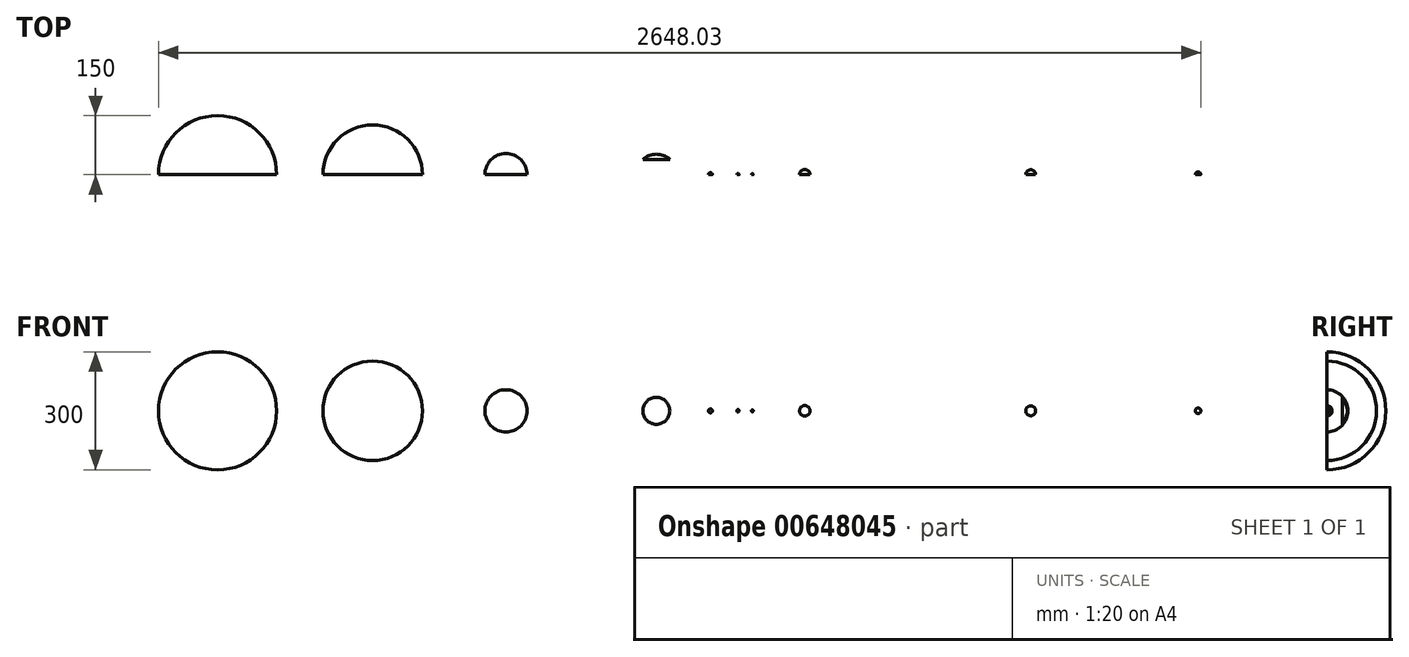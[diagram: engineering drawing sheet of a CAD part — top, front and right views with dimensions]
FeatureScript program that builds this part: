
annotation { "Feature Type Name" : "Feature", "Feature Type Description" : "" }
export const myFeature = defineFeature(function(context is Context, id is Id, definition is map)
    precondition{}
    {
        {
            var Q0;
            Q0=qCreatedBy(makeId("Front.planeOp"),FACE);
            var sketch = newSketch(context, id + "F0", { "sketchPlane" : qUnion([Q0])});
            skArc(sketch, "E0", {"start": v(-1165.18, 0) * mm, "mid": v(-1315.18, 150) * mm, "end": v(-1465.18, 0) * mm});
            skArc(sketch, "E1", {"start": v(-794.77, 0) * mm, "mid": v(-921.23, 126.45) * mm, "end": v(-1047.68, 0) * mm});
            skArc(sketch, "E2", {"start": v(-528.9, 0) * mm, "mid": v(-582.52, 53.63) * mm, "end": v(-636.15, 0) * mm});
            skArc(sketch, "E3", {"start": v(-148.68, 0) * mm, "mid": v(-200.58, 51.9) * mm, "end": v(-252.48, 0) * mm});
            skArc(sketch, "E4", {"start": v(189.86, 0) * mm, "mid": v(176.56, 13.3) * mm, "end": v(163.26, 0) * mm});
            skArc(sketch, "E5", {"start": v(763.27, 0) * mm, "mid": v(750.67, 12.6) * mm, "end": v(738.07, 0) * mm});
            skArc(sketch, "E6", {"start": v(1182.85, 0) * mm, "mid": v(1175.85, 7) * mm, "end": v(1168.85, 0) * mm});
            skLineSegment(sketch, "E7", {"start": v(-1165.18, 0) * mm, "end": v(-1465.18, 0) * mm});
            skLineSegment(sketch, "E8", {"start": v(-1047.68, 0) * mm, "end": v(-794.77, 0) * mm});
            skLineSegment(sketch, "E9", {"start": v(-636.15, 0) * mm, "end": v(-528.9, 0) * mm});
            skLineSegment(sketch, "E10", {"start": v(-252.48, 0) * mm, "end": v(-148.68, 0) * mm});
            skLineSegment(sketch, "E11", {"start": v(163.26, 0) * mm, "end": v(189.86, 0) * mm});
            skLineSegment(sketch, "E12", {"start": v(738.07, 0) * mm, "end": v(763.27, 0) * mm});
            skLineSegment(sketch, "E13", {"start": v(1168.85, 0) * mm, "end": v(1182.85, 0) * mm});
            skArc(sketch, "E14", {"start": v(-58.12, 0) * mm, "mid": v(-63.12, 5) * mm, "end": v(-68.12, 0) * mm});
            skArc(sketch, "E15", {"start": v(9.86, 0) * mm, "mid": v(6.86, 3) * mm, "end": v(3.86, 0) * mm});
            skLineSegment(sketch, "E16", {"start": v(-68.12, 0) * mm, "end": v(-58.12, 0) * mm});
            skLineSegment(sketch, "E17", {"start": v(3.86, 0) * mm, "end": v(9.86, 0) * mm});
            skArc(sketch, "E18", {"start": v(45.8, 0) * mm, "mid": v(43.3, 2.5) * mm, "end": v(40.8, 0) * mm});
            skLineSegment(sketch, "E19", {"start": v(40.8, 0) * mm, "end": v(45.8, 0) * mm});
            skSolve(sketch);
        }
        {
            var Q0;
            Q0=qSketchRegion(id+"F0",true);
            var Q1;
            Q1=sQuery(id+"F0.wireOp",EDGE,"E7");
            revolve(context, id + "F1", {"entities" : qUnion([Q0]), "axis" : qUnion([Q1]), "revolveType" : RevolveType.ONE_DIRECTION, "angle" : 180 * degree});
        }
        {
            var Q0;
            Q0=makeQuery(id+"F0.imprint","IMPRINT",FACE,{"disambiguationData":[TD([[makeQuery(id+"F0.imprint","IMPRINT",EDGE,{"derivedFrom":sQuery(id+"F0.wireOp",EDGE,"E3")}),1.0]])]});
            var sketch = newSketch(context, id + "F2", { "sketchPlane" : qUnion([Q0])});
            skLineSegment(sketch, "E20.bottom", {"start": v(-277.1, 62.55) * mm, "end": v(-132.04, 62.55) * mm});
            skLineSegment(sketch, "E20.top", {"start": v(-277.1, -67.88) * mm, "end": v(-132.04, -67.88) * mm});
            skLineSegment(sketch, "E20.left", {"start": v(-277.1, 62.55) * mm, "end": v(-277.1, -67.88) * mm});
            skLineSegment(sketch, "E20.right", {"start": v(-132.04, 62.55) * mm, "end": v(-132.04, -67.88) * mm});
            skSolve(sketch);
        }
        {
            var Q0;
            Q0 = qSketchRegion(id + "F2", true);
            extrude(context, id + "F3", {"entities" : qUnion([Q0]), "oppositeDirection" : true, "depth" : 39 * mm, "offsetDistance" : 25 * mm});
        }
        {
            var Q0;
            Q0=makeQuery(id+"F3.opExtrude","SWEPT_BODY",BODY,{"disambiguationData":[OSD([sQuery(id+"F2.wireOp",EDGE,"E20.bottom"),sQuery(id+"F2.wireOp",EDGE,"E20.top"),sQuery(id+"F2.wireOp",EDGE,"E20.left"),sQuery(id+"F2.wireOp",EDGE,"E20.right")])]});
            var Q1;
            Q1=makeQuery(id+"F1.opRevolve","SWEPT_BODY",BODY,{"disambiguationData":[OSD([sQuery(id+"F0.wireOp",EDGE,"E3"),sQuery(id+"F0.wireOp",EDGE,"E10")])]});
            booleanBodies(context, id + "F4", {"operationType" : BooleanOperationType.SUBTRACTION, "tools" : qUnion([Q0]), "targets" : qUnion([Q1])});
        }
    });
